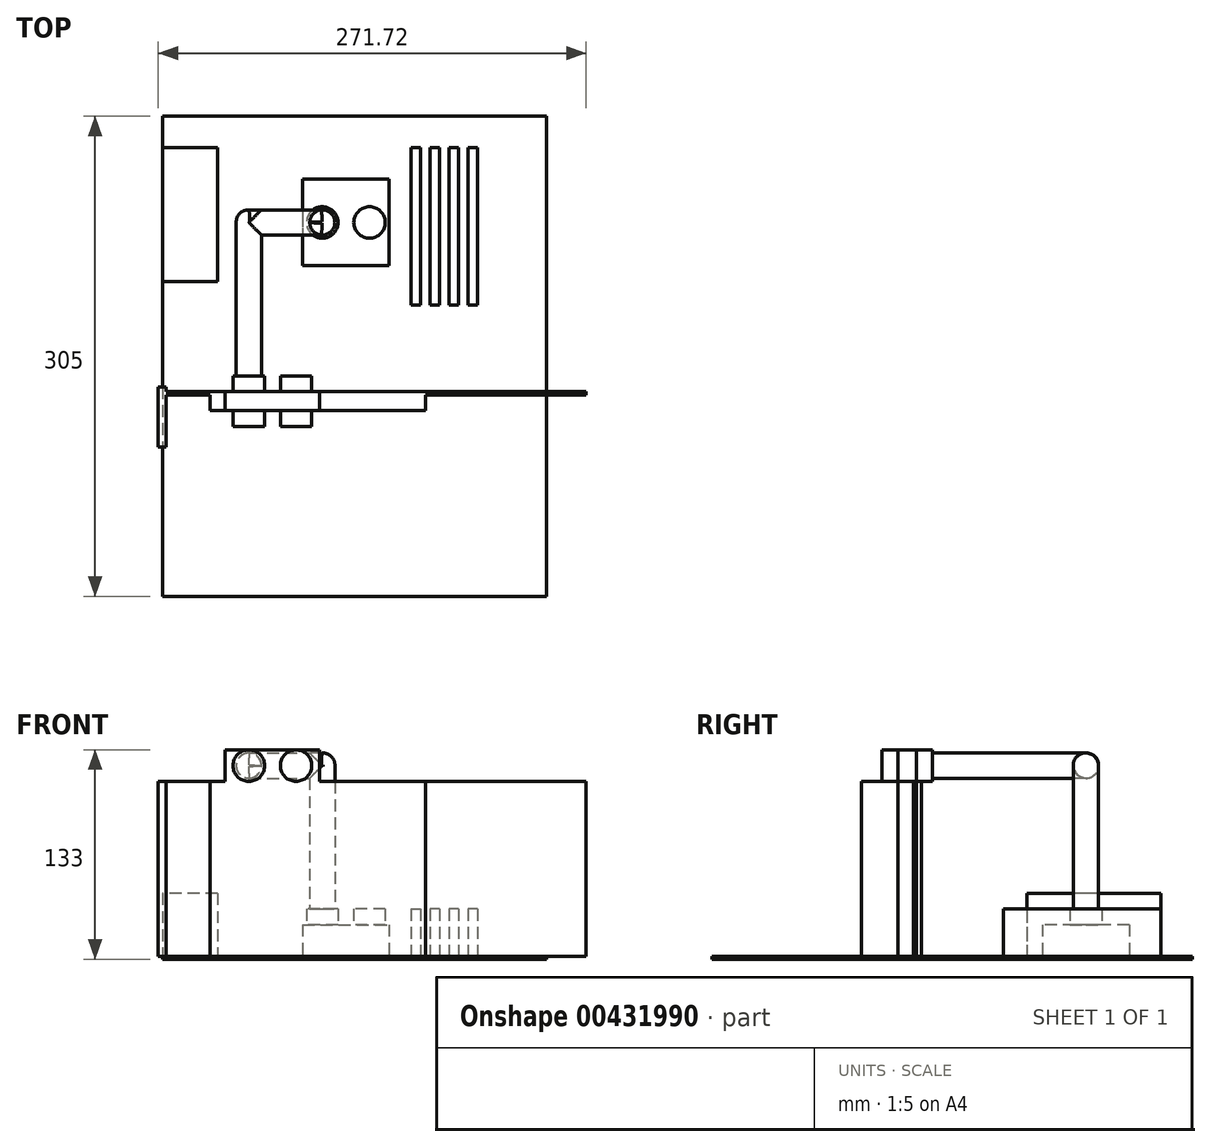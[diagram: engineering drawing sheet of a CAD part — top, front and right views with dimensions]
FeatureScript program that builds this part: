
annotation { "Feature Type Name" : "Feature", "Feature Type Description" : "" }
export const myFeature = defineFeature(function(context is Context, id is Id, definition is map)
    precondition{}
    {
        {
            var Q0;
            Q0=qCreatedBy(makeId("Top.planeOp"),FACE);
            var sketch = newSketch(context, id + "F0", { "sketchPlane" : qUnion([Q0])});
            skLineSegment(sketch, "E0.bottom", {"start": v(-122, 152.5) * mm, "end": v(122, 152.5) * mm});
            skLineSegment(sketch, "E0.top", {"start": v(-122, -152.5) * mm, "end": v(122, -152.5) * mm});
            skLineSegment(sketch, "E0.left", {"start": v(-122, 152.5) * mm, "end": v(-122, -152.5) * mm});
            skLineSegment(sketch, "E0.right", {"start": v(122, 152.5) * mm, "end": v(122, -152.5) * mm});
            skPoint(sketch, "E0.middle", {"position": v(0, 0) * mm});
            skSolve(sketch);
        }
        {
            var Q0;
            Q0=makeQuery(id+"F0.imprint","IMPRINT",FACE,{"disambiguationData":[TD([[makeQuery(id+"F0.imprint","IMPRINT",EDGE,{"derivedFrom":sQuery(id+"F0.wireOp",EDGE,"E0.bottom")}),-1.0]])]});
            extrude(context, id + "F1", {"entities" : qUnion([Q0]), "depth" : 2 * mm});
        }
        {
            var Q0;
            Q0=makeQuery(id+"F1.opExtrude","CAP_FACE",FACE,{"disambiguationData":[OSD([sQuery(id+"F0.wireOp",EDGE,"E0.bottom"),sQuery(id+"F0.wireOp",EDGE,"E0.top"),sQuery(id+"F0.wireOp",EDGE,"E0.left"),sQuery(id+"F0.wireOp",EDGE,"E0.right")])],"isStart":false});
            var sketch = newSketch(context, id + "F2", { "sketchPlane" : qUnion([Q0])});
            skLineSegment(sketch, "E1.bottom", {"start": v(-33, 112.5) * mm, "end": v(22, 112.5) * mm});
            skLineSegment(sketch, "E1.top", {"start": v(-33, 57.5) * mm, "end": v(22, 57.5) * mm});
            skLineSegment(sketch, "E1.left", {"start": v(-33, 112.5) * mm, "end": v(-33, 57.5) * mm});
            skLineSegment(sketch, "E1.right", {"start": v(22, 112.5) * mm, "end": v(22, 57.5) * mm});
            skPoint(sketch, "E1.middle", {"position": v(-5.5, 85) * mm});
            skSolve(sketch);
        }
        {
            var Q0;
            Q0=qSketchRegion(id+"F2",true);
            extrude(context, id + "F3", {"entities" : qUnion([Q0]), "operationType" : NewBodyOperationType.ADD, "depth" : 20 * mm});
        }
        {
            var Q0;
            Q0=makeQuery(id+"F1.opExtrude","CAP_FACE",FACE,{"disambiguationData":[OSD([sQuery(id+"F0.wireOp",EDGE,"E0.bottom"),sQuery(id+"F0.wireOp",EDGE,"E0.top"),sQuery(id+"F0.wireOp",EDGE,"E0.left"),sQuery(id+"F0.wireOp",EDGE,"E0.right")])],"isStart":false});
            var sketch = newSketch(context, id + "F4", { "sketchPlane" : qUnion([Q0])});
            skLineSegment(sketch, "E2.bottom", {"start": v(36, 132.5) * mm, "end": v(42, 132.5) * mm});
            skLineSegment(sketch, "E2.top", {"start": v(36, 32.5) * mm, "end": v(42, 32.5) * mm});
            skLineSegment(sketch, "E2.left", {"start": v(36, 132.5) * mm, "end": v(36, 32.5) * mm});
            skLineSegment(sketch, "E2.right", {"start": v(42, 132.5) * mm, "end": v(42, 32.5) * mm});
            skPoint(sketch, "E2.middle", {"position": v(39.37, 85) * mm});
            skPoint(sketch, "E2.middle.positionSnap0", {"position": v(22, 85) * mm});
            skPoint(sketch, "E2.centerSnap0", {"position": v(22, 85) * mm});
            skLineSegment(sketch, "E3.bottom", {"start": v(54, 132.5) * mm, "end": v(48, 132.5) * mm});
            skLineSegment(sketch, "E3.top", {"start": v(54, 32.5) * mm, "end": v(48, 32.5) * mm});
            skLineSegment(sketch, "E3.left", {"start": v(54, 132.5) * mm, "end": v(54, 32.5) * mm});
            skLineSegment(sketch, "E3.right", {"start": v(48, 132.5) * mm, "end": v(48, 32.5) * mm});
            skPoint(sketch, "E3.middle", {"position": v(51, 82.5) * mm});
            skPoint(sketch, "E3.middle.positionSnap0", {"position": v(42, 82.5) * mm});
            skPoint(sketch, "E3.centerSnap0", {"position": v(42, 82.5) * mm});
            skLineSegment(sketch, "E4.bottom", {"start": v(66, 132.5) * mm, "end": v(60, 132.5) * mm});
            skLineSegment(sketch, "E4.top", {"start": v(66, 32.5) * mm, "end": v(60, 32.5) * mm});
            skLineSegment(sketch, "E4.left", {"start": v(66, 132.5) * mm, "end": v(66, 32.5) * mm});
            skLineSegment(sketch, "E4.right", {"start": v(60, 132.5) * mm, "end": v(60, 32.5) * mm});
            skPoint(sketch, "E4.middle", {"position": v(63, 82.5) * mm});
            skPoint(sketch, "E4.middle.positionSnap0", {"position": v(54, 82.5) * mm});
            skPoint(sketch, "E4.centerSnap0", {"position": v(54, 82.5) * mm});
            skLineSegment(sketch, "E5.bottom", {"start": v(78, 132.5) * mm, "end": v(72, 132.5) * mm});
            skLineSegment(sketch, "E5.top", {"start": v(78, 32.5) * mm, "end": v(72, 32.5) * mm});
            skLineSegment(sketch, "E5.left", {"start": v(78, 132.5) * mm, "end": v(78, 32.5) * mm});
            skLineSegment(sketch, "E5.right", {"start": v(72, 132.5) * mm, "end": v(72, 32.5) * mm});
            skPoint(sketch, "E5.middle", {"position": v(75, 82.5) * mm});
            skPoint(sketch, "E5.middle.positionSnap0", {"position": v(66, 82.5) * mm});
            skPoint(sketch, "E5.centerSnap0", {"position": v(66, 82.5) * mm});
            skSolve(sketch);
        }
        {
            var Q0;
            Q0=qSketchRegion(id+"F4",true);
            extrude(context, id + "F5", {"entities" : qUnion([Q0]), "operationType" : NewBodyOperationType.ADD, "depth" : 30 * mm});
        }
        {
            var Q0;
            Q0=makeQuery(id+"F1.opExtrude","CAP_FACE",FACE,{"disambiguationData":[OSD([sQuery(id+"F0.wireOp",EDGE,"E0.bottom"),sQuery(id+"F0.wireOp",EDGE,"E0.top"),sQuery(id+"F0.wireOp",EDGE,"E0.left"),sQuery(id+"F0.wireOp",EDGE,"E0.right")])],"isStart":false});
            var sketch = newSketch(context, id + "F6", { "sketchPlane" : qUnion([Q0])});
            skLineSegment(sketch, "E6.bottom", {"start": v(-87, 132.5) * mm, "end": v(-122, 132.5) * mm});
            skLineSegment(sketch, "E6.top", {"start": v(-87, 47.5) * mm, "end": v(-122, 47.5) * mm});
            skLineSegment(sketch, "E6.left", {"start": v(-87, 132.5) * mm, "end": v(-87, 47.5) * mm});
            skLineSegment(sketch, "E6.right", {"start": v(-122, 132.5) * mm, "end": v(-122, 47.5) * mm});
            skSolve(sketch);
        }
        {
            var Q0;
            Q0=qSketchRegion(id+"F6",true);
            extrude(context, id + "F7", {"entities" : qUnion([Q0]), "operationType" : NewBodyOperationType.ADD, "depth" : 40 * mm});
        }
        {
            var Q0;
            Q0=makeQuery(id+"F1.opExtrude","CAP_FACE",FACE,{"disambiguationData":[OSD([sQuery(id+"F0.wireOp",EDGE,"E0.bottom"),sQuery(id+"F0.wireOp",EDGE,"E0.top"),sQuery(id+"F0.wireOp",EDGE,"E0.left"),sQuery(id+"F0.wireOp",EDGE,"E0.right")])],"isStart":false});
            var sketch = newSketch(context, id + "F8", { "sketchPlane" : qUnion([Q0])});
            skLineSegment(sketch, "E7.bottom", {"start": v(-122, -22.5) * mm, "end": v(147, -22.5) * mm});
            skLineSegment(sketch, "E7.top", {"start": v(-122, -24.5) * mm, "end": v(147, -24.5) * mm});
            skLineSegment(sketch, "E7.left", {"start": v(-122, -22.5) * mm, "end": v(-122, -24.5) * mm});
            skLineSegment(sketch, "E7.right", {"start": v(147, -22.5) * mm, "end": v(147, -24.5) * mm});
            skSolve(sketch);
        }
        {
            var Q0;
            Q0=qSketchRegion(id+"F8",true);
            extrude(context, id + "F9", {"entities" : qUnion([Q0]), "operationType" : NewBodyOperationType.ADD, "depth" : 111 * mm});
        }
        {
            var Q0;
            Q0=makeQuery(id+"F9.opExtrude","SWEPT_FACE",FACE,{"disambiguationData":[OSD([sQuery(id+"F8.wireOp",EDGE,"E7.top")])]});
            var sketch = newSketch(context, id + "F10", { "sketchPlane" : qUnion([Q0])});
            skLineSegment(sketch, "E8.bottom", {"start": v(-91.77, 113) * mm, "end": v(45.01, 113) * mm});
            skLineSegment(sketch, "E8.top", {"start": v(-91.77, 2) * mm, "end": v(45.01, 2) * mm});
            skLineSegment(sketch, "E8.left", {"start": v(-91.77, 113) * mm, "end": v(-91.77, 2) * mm});
            skLineSegment(sketch, "E8.right", {"start": v(45.01, 113) * mm, "end": v(45.01, 2) * mm});
            skSolve(sketch);
        }
        {
            var Q0;
            Q0=qSketchRegion(id+"F10",true);
            extrude(context, id + "F11", {"entities" : qUnion([Q0]), "operationType" : NewBodyOperationType.ADD, "depth" : 10 * mm});
        }
        {
            var Q0;
            {var subQ0=sQuery(id+"F0.wireOp",EDGE,"E0.left");var subQ2=sQuery(id+"F8.wireOp",EDGE,"E7.top");Q0=makeQuery(id+"F11.boolean.opBoolean","SPLIT",FACE,{"disambiguationData":[TD([makeQuery(id+"F1.opExtrude","SWEPT_FACE",FACE,{"disambiguationData":[OSD([subQ0])]})])],"derivedFrom":makeQuery(id+"F9.opExtrude","SWEPT_FACE",FACE,{"disambiguationData":[OSD([subQ2])]})});}
            var sketch = newSketch(context, id + "F12", { "sketchPlane" : qUnion([Q0])});
            skLineSegment(sketch, "E9.bottom", {"start": v(-119.66, 113) * mm, "end": v(-124.72, 113) * mm});
            skLineSegment(sketch, "E9.top", {"start": v(-119.66, 2) * mm, "end": v(-124.72, 2) * mm});
            skLineSegment(sketch, "E9.left", {"start": v(-119.66, 113) * mm, "end": v(-119.66, 2) * mm});
            skLineSegment(sketch, "E9.right", {"start": v(-124.72, 113) * mm, "end": v(-124.72, 2) * mm});
            skSolve(sketch);
        }
        {
            var Q0;
            Q0=qSketchRegion(id+"F12",true);
            extrude(context, id + "F13", {"entities" : qUnion([Q0]), "operationType" : NewBodyOperationType.ADD, "depth" : 33 * mm, "hasSecondDirection" : true, "secondDirectionOppositeDirection" : true, "secondDirectionDepth" : 5 * mm});
        }
        {
            var Q0;
            Q0=makeQuery(id+"F13.boolean.opBoolean","MERGE",FACE,{"derivedFrom":[makeQuery(id+"F11.boolean.opBoolean","MERGE",FACE,{"derivedFrom":[makeQuery(id+"F9.opExtrude","CAP_FACE",FACE,{"disambiguationData":[OSD([sQuery(id+"F8.wireOp",EDGE,"E7.bottom"),sQuery(id+"F8.wireOp",EDGE,"E7.top"),sQuery(id+"F8.wireOp",EDGE,"E7.left"),sQuery(id+"F8.wireOp",EDGE,"E7.right")])],"isStart":false}),makeQuery(id+"F11.opExtrude","SWEPT_FACE",FACE,{"disambiguationData":[OSD([sQuery(id+"F10.wireOp",EDGE,"E8.bottom")])]})]}),makeQuery(id+"F13.opExtrude","SWEPT_FACE",FACE,{"disambiguationData":[OSD([sQuery(id+"F12.wireOp",EDGE,"E9.bottom")])]})]});
            var sketch = newSketch(context, id + "F14", { "sketchPlane" : qUnion([Q0])});
            skLineSegment(sketch, "E10.bottom", {"start": v(-82.15, -22.5) * mm, "end": v(-22.15, -22.5) * mm});
            skLineSegment(sketch, "E10.top", {"start": v(-82.15, -34.5) * mm, "end": v(-22.15, -34.5) * mm});
            skLineSegment(sketch, "E10.left", {"start": v(-82.15, -22.5) * mm, "end": v(-82.15, -34.5) * mm});
            skLineSegment(sketch, "E10.right", {"start": v(-22.15, -22.5) * mm, "end": v(-22.15, -34.5) * mm});
            skSolve(sketch);
        }
        {
            var Q0;
            Q0=qSketchRegion(id+"F14",true);
            extrude(context, id + "F15", {"entities" : qUnion([Q0]), "operationType" : NewBodyOperationType.ADD, "depth" : 20 * mm});
        }
        {
            var Q0;
            Q0=makeQuery(id+"F3.opExtrude","CAP_FACE",FACE,{"disambiguationData":[OSD([sQuery(id+"F2.wireOp",EDGE,"E1.bottom"),sQuery(id+"F2.wireOp",EDGE,"E1.top"),sQuery(id+"F2.wireOp",EDGE,"E1.left"),sQuery(id+"F2.wireOp",EDGE,"E1.right")])],"isStart":false});
            var sketch = newSketch(context, id + "F16", { "sketchPlane" : qUnion([Q0])});
            skLineSegment(sketch, "E11", {"start": v(-5.5, 57.5) * mm, "end": v(-5.5, 112.5) * mm, "construction": true});
            skLineSegment(sketch, "E12", {"start": v(22, 85) * mm, "end": v(-33, 85) * mm, "construction": true});
            skCircle(sketch, "E13", {"center": v(-20.5, 85) * mm, "radius": 10 * mm});
            skCircle(sketch, "E14.MirrorC", {"center": v(9.5, 85) * mm, "radius": 10 * mm});
            skSolve(sketch);
        }
        {
            var Q0;
            Q0=qSketchRegion(id+"F16",true);
            extrude(context, id + "F17", {"entities" : qUnion([Q0]), "operationType" : NewBodyOperationType.ADD, "depth" : 10 * mm});
        }
        {
            var Q0;
            Q0=makeQuery(id+"F15.boolean.opBoolean","MERGE",FACE,{"derivedFrom":[makeQuery(id+"F11.opExtrude","CAP_FACE",FACE,{"disambiguationData":[OSD([sQuery(id+"F10.wireOp",EDGE,"E8.bottom"),sQuery(id+"F10.wireOp",EDGE,"E8.top"),sQuery(id+"F10.wireOp",EDGE,"E8.left"),sQuery(id+"F10.wireOp",EDGE,"E8.right")])],"isStart":false}),makeQuery(id+"F15.opExtrude","SWEPT_FACE",FACE,{"disambiguationData":[OSD([sQuery(id+"F14.wireOp",EDGE,"E10.top")])]})]});
            var sketch = newSketch(context, id + "F18", { "sketchPlane" : qUnion([Q0])});
            skCircle(sketch, "E15", {"center": v(-67.15, 123) * mm, "radius": 10 * mm});
            skLineSegment(sketch, "E16", {"start": v(-82.15, 123) * mm, "end": v(-22.15, 123) * mm, "construction": true});
            skLineSegment(sketch, "E17", {"start": v(-52.15, 133) * mm, "end": v(-52.15, 123) * mm, "construction": true});
            skCircle(sketch, "E18.MirrorC", {"center": v(-37.15, 123) * mm, "radius": 10 * mm});
            skSolve(sketch);
        }
        {
            var Q0;
            Q0=qSketchRegion(id+"F18",true);
            extrude(context, id + "F19", {"entities" : qUnion([Q0]), "operationType" : NewBodyOperationType.ADD, "depth" : 10 * mm});
        }
        {
            var Q0;
            Q0=makeQuery(id+"F15.boolean.opBoolean","MERGE",FACE,{"derivedFrom":[makeQuery(id+"F9.opExtrude","SWEPT_FACE",FACE,{"disambiguationData":[OSD([sQuery(id+"F8.wireOp",EDGE,"E7.bottom")])]}),makeQuery(id+"F15.opExtrude","SWEPT_FACE",FACE,{"disambiguationData":[OSD([sQuery(id+"F14.wireOp",EDGE,"E10.bottom")])]})]});
            var sketch = newSketch(context, id + "F20", { "sketchPlane" : qUnion([Q0])});
            skLineSegment(sketch, "E19", {"start": v(22.15, 123) * mm, "end": v(82.15, 123) * mm, "construction": true});
            skLineSegment(sketch, "E20", {"start": v(52.15, 133) * mm, "end": v(52.15, 123) * mm, "construction": true});
            skCircle(sketch, "E21", {"center": v(37.15, 123) * mm, "radius": 10 * mm});
            skCircle(sketch, "E22.MirrorC", {"center": v(67.15, 123) * mm, "radius": 10 * mm});
            skSolve(sketch);
        }
        {
            var Q0;
            Q0=qSketchRegion(id+"F20",true);
            extrude(context, id + "F21", {"entities" : qUnion([Q0]), "operationType" : NewBodyOperationType.ADD, "depth" : 10 * mm});
        }
        {
            var Q0;
            Q0=makeQuery(id+"F21.opExtrude","CAP_FACE",FACE,{"disambiguationData":[OSD([sQuery(id+"F20.wireOp",EDGE,"E22.MirrorC")])],"isStart":false});
            var sketch = newSketch(context, id + "F22", { "sketchPlane" : qUnion([Q0])});
            skCircle(sketch, "E23", {"center": v(67.15, 123) * mm, "radius": 8 * mm});
            skSolve(sketch);
        }
        {
            var Q0;
            Q0=qSketchRegion(id+"F22",true);
            extrude(context, id + "F23", {"entities" : qUnion([Q0]), "operationType" : NewBodyOperationType.ADD, "depth" : 105.5 * mm});
        }
        {
            var Q0;
            Q0=makeQuery(id+"F17.opExtrude","CAP_FACE",FACE,{"disambiguationData":[OSD([sQuery(id+"F16.wireOp",EDGE,"E13")])],"isStart":false});
            var sketch = newSketch(context, id + "F24", { "sketchPlane" : qUnion([Q0])});
            skCircle(sketch, "E24", {"center": v(-20.5, 85) * mm, "radius": 8 * mm});
            skSolve(sketch);
        }
        {
            var Q0;
            Q0=qSketchRegion(id+"F24",true);
            extrude(context, id + "F25", {"entities" : qUnion([Q0]), "operationType" : NewBodyOperationType.ADD, "depth" : 99 * mm});
        }
        {
            var Q0;
            Q0=qCreatedBy(makeId("Right.planeOp"),FACE);
            cPlane(context, id + "F26", {"entities" : qUnion([Q0]), "cplaneType" : CPlaneType.OFFSET, "offset" : 20 * mm, "oppositeDirection" : true, "width" : 150 * mm, "height" : 150 * mm});
        }
        {
            var Q0;
            Q0=qCreatedBy(id+"F26.planeOp",FACE);
            var sketch = newSketch(context, id + "F27", { "sketchPlane" : qUnion([Q0])});
            skCircle(sketch, "E25", {"center": v(85, 123) * mm, "radius": 8 * mm});
            skLineSegment(sketch, "E26.0", {"start": v(77, 131) * mm, "end": v(93, 131) * mm, "construction": true});
            skLineSegment(sketch, "E27", {"start": v(85, 131) * mm, "end": v(85, 123) * mm, "construction": true});
            skSolve(sketch);
        }
        {
            var Q0;
            Q0=qSketchRegion(id+"F27",true);
            extrude(context, id + "F28", {"entities" : qUnion([Q0]), "operationType" : NewBodyOperationType.ADD, "oppositeDirection" : true, "depth" : 47 * mm});
        }
        {
            var Q0;
            Q0=makeQuery(id+"F25.opExtrude","CAP_EDGE",EDGE,{"disambiguationData":[OSD([sQuery(id+"F24.wireOp",EDGE,"E24")])],"isStart":false});
            fillet(context, id + "F29", {"entities" : qUnion([Q0]), "radius" : 7.5 * mm, "tangentPropagation" : true, "allowEdgeOverflow" : false});
        }
        {
            var Q0;
            Q0=makeQuery(id+"F23.opExtrude","CAP_EDGE",EDGE,{"disambiguationData":[OSD([sQuery(id+"F22.wireOp",EDGE,"E23")])],"isStart":false});
            fillet(context, id + "F30", {"entities" : qUnion([Q0]), "radius" : 7.5 * mm, "tangentPropagation" : true, "allowEdgeOverflow" : false});
        }
    });
